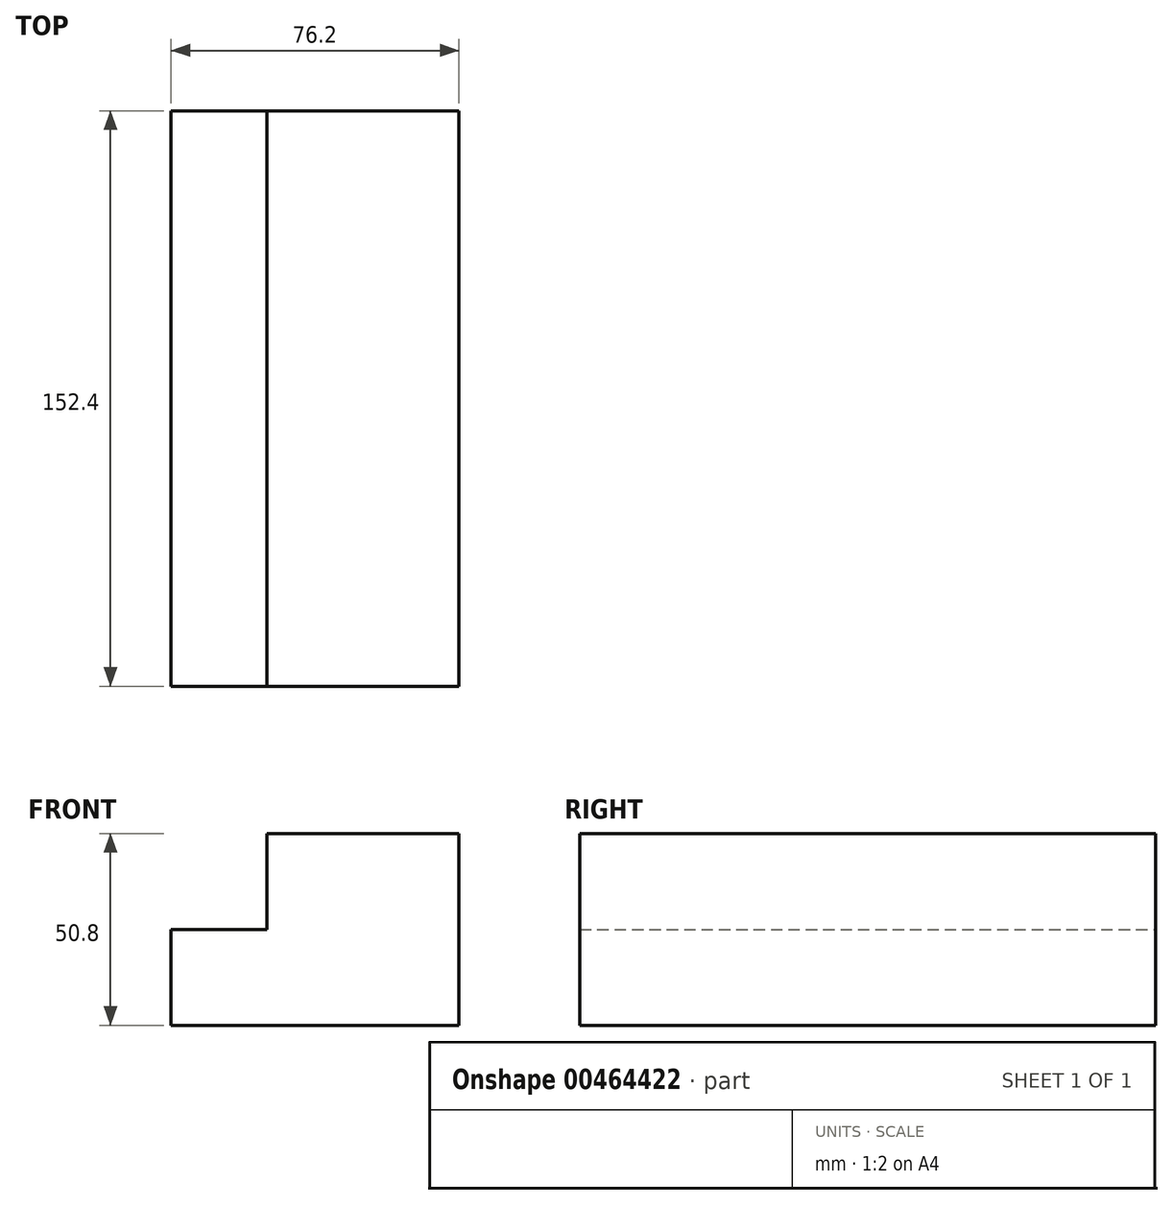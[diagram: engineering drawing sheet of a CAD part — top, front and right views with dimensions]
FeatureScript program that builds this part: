
annotation { "Feature Type Name" : "Feature", "Feature Type Description" : "" }
export const myFeature = defineFeature(function(context is Context, id is Id, definition is map)
    precondition{}
    {
        {
            var Q0;
            Q0=qCreatedBy(makeId("Front.planeOp"),FACE);
            var sketch = newSketch(context, id + "F0", { "sketchPlane" : qUnion([Q0])});
            skLineSegment(sketch, "E0", {"start": v(72.05, 61.67) * mm, "end": v(21.25, 61.67) * mm});
            skLineSegment(sketch, "E1", {"start": v(21.25, 61.67) * mm, "end": v(21.25, 36.27) * mm});
            skLineSegment(sketch, "E2", {"start": v(21.25, 36.27) * mm, "end": v(-4.15, 36.27) * mm});
            skLineSegment(sketch, "E3", {"start": v(-4.15, 36.27) * mm, "end": v(-4.15, 10.87) * mm});
            skLineSegment(sketch, "E4", {"start": v(-4.15, 10.87) * mm, "end": v(72.05, 10.87) * mm});
            skLineSegment(sketch, "E5", {"start": v(72.05, 10.87) * mm, "end": v(72.05, 61.67) * mm});
            skSolve(sketch);
        }
        {
            var Q0;
            Q0=makeQuery(id+"F0.imprint","IMPRINT",FACE,{"disambiguationData":[TD([[makeQuery(id+"F0.imprint","IMPRINT",EDGE,{"derivedFrom":sQuery(id+"F0.wireOp",EDGE,"E0")}),1.0]])]});
            extrude(context, id + "F1", {"entities" : qUnion([Q0]), "depth" : 152.4 * mm});
        }
    });
